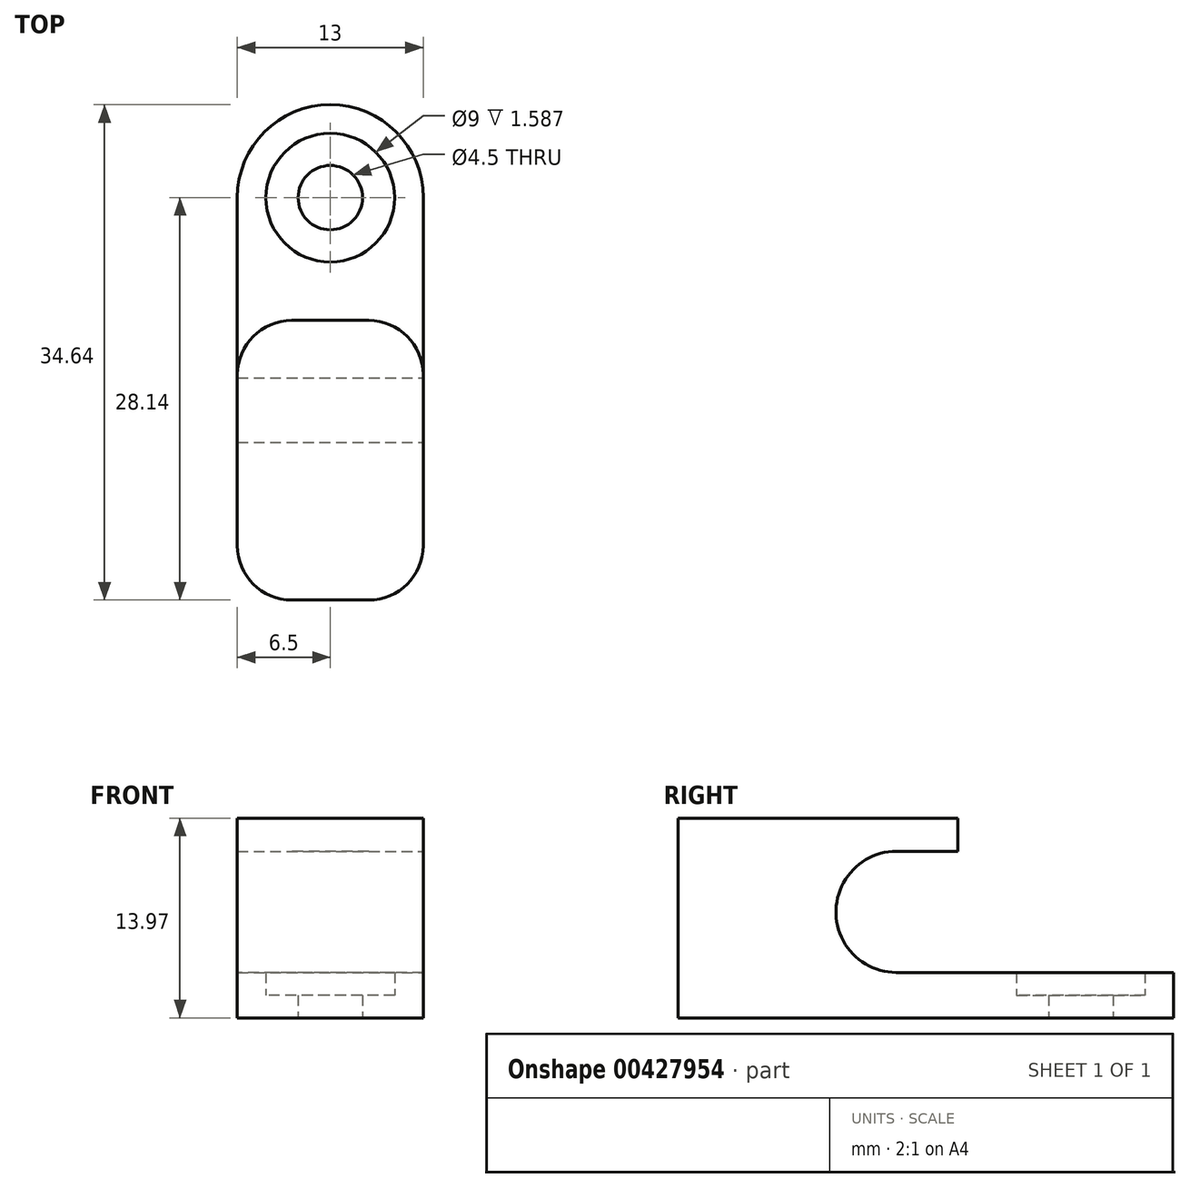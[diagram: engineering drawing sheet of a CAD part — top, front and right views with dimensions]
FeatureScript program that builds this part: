
annotation { "Feature Type Name" : "Feature", "Feature Type Description" : "" }
export const myFeature = defineFeature(function(context is Context, id is Id, definition is map)
    precondition{}
    {
        {
            var Q0;
            Q0=qCreatedBy(makeId("Top.planeOp"),FACE);
            var sketch = newSketch(context, id + "F0", { "sketchPlane" : qUnion([Q0])});
            skCircle(sketch, "E0", {"center": v(0, 0) * mm, "radius": 2.25 * mm});
            skCircle(sketch, "E1", {"center": v(0, 0) * mm, "radius": 4.5 * mm});
            skCircle(sketch, "E2", {"center": v(0, 0) * mm, "radius": 6.5 * mm});
            skLineSegment(sketch, "E3.top", {"start": v(-2.69, -28.14) * mm, "end": v(2.69, -28.14) * mm});
            skLineSegment(sketch, "E3.left", {"start": v(-6.5, 0) * mm, "end": v(-6.5, -24.33) * mm});
            skLineSegment(sketch, "E3.right", {"start": v(6.5, 0) * mm, "end": v(6.5, -24.33) * mm});
            skPoint(sketch, "E4.visualSharp", {"position": v(-6.5, -28.14) * mm});
            skArc(sketch, "E4.filletArc", {"start": v(-6.5, -24.33) * mm, "mid": v(-5.38, -27.03) * mm, "end": v(-2.69, -28.14) * mm});
            skPoint(sketch, "E5.visualSharp", {"position": v(6.5, -28.14) * mm});
            skArc(sketch, "E5.filletArc", {"start": v(2.69, -28.14) * mm, "mid": v(5.38, -27.03) * mm, "end": v(6.5, -24.33) * mm});
            skLineSegment(sketch, "E6", {"start": v(-6.5, -8.59) * mm, "end": v(6.5, -8.59) * mm});
            skSolve(sketch);
        }
        {
            var Q0;
            {var subQ5=sQuery(id+"F0.wireOp",EDGE,"E6");Q0=makeQuery(id+"F0.imprint","IMPRINT",FACE,{"disambiguationData":[TD([[makeQuery(id+"F0.imprint","IMPRINT",EDGE,{"derivedFrom":subQ5}),1.0]])]});}
            var Q1;
            Q1=makeQuery(id+"F0.imprint","IMPRINT",FACE,{"disambiguationData":[TD([[makeQuery(id+"F0.imprint","IMPRINT",EDGE,{"derivedFrom":sQuery(id+"F0.wireOp",EDGE,"E1")}),-1.0]])]});
            extrude(context, id + "F1", {"entities" : qUnion([Q0, Q1]), "depth" : 3.17 * mm});
        }
        {
            var Q0;
            Q0=makeQuery(id+"F0.imprint","IMPRINT",FACE,{"disambiguationData":[TD([[makeQuery(id+"F0.imprint","IMPRINT",EDGE,{"derivedFrom":sQuery(id+"F0.wireOp",EDGE,"E0")}),-1.0]])]});
            extrude(context, id + "F2", {"entities" : qUnion([Q0]), "operationType" : NewBodyOperationType.ADD, "depth" : 1.59 * mm});
        }
        {
            var Q0;
            Q0=makeQuery(id+"F0.imprint","IMPRINT",FACE,{"disambiguationData":[TD([[makeQuery(id+"F0.imprint","IMPRINT",EDGE,{"derivedFrom":sQuery(id+"F0.wireOp",EDGE,"E3.top")}),1.0]])]});
            extrude(context, id + "F3", {"entities" : qUnion([Q0]), "operationType" : NewBodyOperationType.ADD, "depth" : 13.97 * mm});
        }
        {
            var Q0;
            {var subQ0=sQuery(id+"F0.wireOp",EDGE,"E3.right");Q0=makeQuery(id+"F3.boolean.opBoolean","MERGE",FACE,{"derivedFrom":[makeQuery(id+"F1.opExtrude","SWEPT_FACE",FACE,{"disambiguationData":[OSD([subQ0])]}),makeQuery(id+"F3.opExtrude","SWEPT_FACE",FACE,{"disambiguationData":[OSD([subQ0])]})]});}
            var sketch = newSketch(context, id + "F4", { "sketchPlane" : qUnion([Q0])});
            skLineSegment(sketch, "E7", {"start": v(0, 3.18) * mm, "end": v(-22.53, 3.18) * mm, "construction": true});
            skCircle(sketch, "E8", {"center": v(-12.87, 7.4) * mm, "radius": 4.24 * mm});
            skLineSegment(sketch, "E9.bottom", {"start": v(-12.87, 11.65) * mm, "end": v(0, 11.65) * mm});
            skLineSegment(sketch, "E9.top", {"start": v(-12.87, 3.18) * mm, "end": v(0, 3.18) * mm});
            skLineSegment(sketch, "E9.left", {"start": v(-12.87, 11.65) * mm, "end": v(-12.87, 3.18) * mm});
            skLineSegment(sketch, "E9.right", {"start": v(0, 11.65) * mm, "end": v(0, 3.18) * mm});
            skSolve(sketch);
        }
        {
            var Q0;
            {var subQ0=sQuery(id+"F4.wireOp",EDGE,"E9.left");var subQ1=sQuery(id+"F4.wireOp",EDGE,"E8");var subQ3=makeQuery(id+"F4.imprint","INTERSECT",VERTEX,{"derivedFrom":[subQ1,subQ0]});Q0=makeQuery(id+"F4.imprint","IMPRINT",FACE,{"disambiguationData":[TD([[makeQuery(id+"F4.imprint","IMPRINT",EDGE,{"disambiguationData":[TD([[subQ3,1.0]])],"derivedFrom":subQ1}),1.0]])]});}
            var Q1;
            {var subQ0=sQuery(id+"F4.wireOp",EDGE,"E9.left");var subQ1=sQuery(id+"F4.wireOp",EDGE,"E8");var subQ3=makeQuery(id+"F4.imprint","INTERSECT",VERTEX,{"derivedFrom":[subQ1,subQ0]});Q1=makeQuery(id+"F4.imprint","IMPRINT",FACE,{"disambiguationData":[TD([[makeQuery(id+"F4.imprint","IMPRINT",EDGE,{"disambiguationData":[TD([[subQ3,-1.0]])],"derivedFrom":subQ1}),1.0]])]});}
            var Q2;
            {var subQ0=sQuery(id+"F4.wireOp",EDGE,"E9.top");var subQ3=sQuery(id+"F4.wireOp",EDGE,"E9.left");var subQ4=makeQuery(id+"F4.imprint","INTERSECT",VERTEX,{"derivedFrom":[subQ0,subQ3]});Q2=makeQuery(id+"F4.imprint","IMPRINT",FACE,{"disambiguationData":[TD([[makeQuery(id+"F4.imprint","IMPRINT",EDGE,{"disambiguationData":[TD([[subQ4,1.0]])],"derivedFrom":subQ3}),1.0]])]});}
            var Q3;
            {var subQ0=sQuery(id+"F4.wireOp",EDGE,"E9.right");Q3=makeQuery(id+"F4.imprint","IMPRINT",FACE,{"disambiguationData":[TD([[makeQuery(id+"F4.imprint","IMPRINT",EDGE,{"derivedFrom":subQ0}),-1.0]])]});}
            var Q4;
            {var subQ1=sQuery(id+"F4.wireOp",EDGE,"E8");var subQ3=sQuery(id+"F4.wireOp",EDGE,"E9.top");var subQ4=makeQuery(id+"F4.imprint","INTERSECT",VERTEX,{"derivedFrom":[subQ1,subQ3]});Q4=makeQuery(id+"F4.imprint","IMPRINT",FACE,{"disambiguationData":[TD([[makeQuery(id+"F4.imprint","IMPRINT",EDGE,{"disambiguationData":[TD([[subQ4,-1.0]])],"derivedFrom":subQ1}),-1.0]])]});}
            extrude(context, id + "F5", {"entities" : qUnion([Q0, Q1, Q2, Q3, Q4]), "operationType" : NewBodyOperationType.REMOVE, "oppositeDirection" : true, "depth" : 25.4 * mm});
        }
        {
            var Q0;
            Q0=makeQuery(id+"F3.opExtrude","SWEPT_EDGE",EDGE,{"disambiguationData":[OSD([sQuery(id+"F0.wireOp",EDGE,"E3.right"),sQuery(id+"F0.wireOp",EDGE,"E6")])]});
            var Q1;
            Q1=makeQuery(id+"F3.opExtrude","SWEPT_EDGE",EDGE,{"disambiguationData":[OSD([sQuery(id+"F0.wireOp",EDGE,"E3.left"),sQuery(id+"F0.wireOp",EDGE,"E6")])]});
            fillet(context, id + "F6", {"entities" : qUnion([Q0, Q1]), "radius" : 3.8 * mm, "tangentPropagation" : true, "allowEdgeOverflow" : false});
        }
    });
